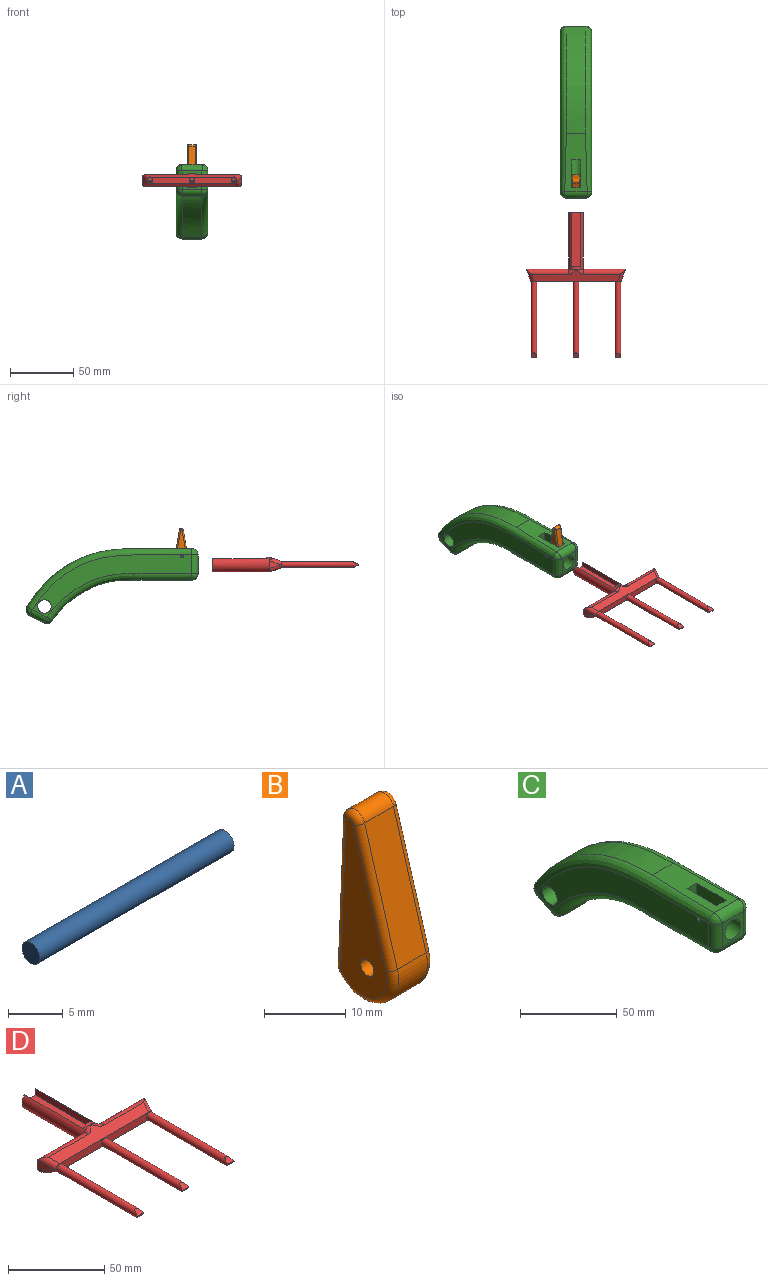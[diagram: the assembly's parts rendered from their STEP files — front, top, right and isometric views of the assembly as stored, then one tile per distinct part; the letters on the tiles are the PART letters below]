
ASSEMBLY  parts=4 mates=3
PART A: 3 faces, bbox 25x2.3x2.3 mm
  f0: cylinder r=1.14mm len=25mm, axis (1,0,0), area 179.2mm2, adj f1,f2
  f1: plane 2.28x2.28mm, normal (-1,0,0), area 4.1mm2, adj f0
  f2: plane 2.28x2.28mm, normal (1,0,0), area 4.1mm2, adj f0
PART B: 15 faces, bbox 7x10.9x27.8 mm
  f0: plane 19.22x5.69mm, normal (0,-0.96,0.28), area 100.2mm2, adj f1,f3,f8,f12
  f1: cylinder r=5.38mm len=10.09mm, axis (-1,0,0), area 78.7mm2, adj f0,f2,f10,f14
  f2: plane 23.45x5mm, normal (0,1,0.04), area 117.4mm2, adj f1,f3,f9,f13
  f3: cylinder r=1.69mm len=5mm, axis (-1,0,0), area 21.2mm2, adj f0,f2,f7,f11
  f4: plane 25.34x8.08mm, normal (1,0,0), area 121.9mm2, adj f6,f11,f12,f13,f14
  f5: plane 25.34x8.08mm, normal (-1,0,0), area 121.9mm2, adj f6,f7,f8,f9,f10
  f6: cylinder r=1.14mm len=7mm, axis (-1,0,0), area 50.2mm2, adj f4,f5
  f7: torus R=0.69mm, axis (1,0,0), area 5.1mm2, adj f3,f5,f8,f9
  f8: cylinder r=1mm len=19.5mm, axis (0,-0.28,-0.96), area 31.5mm2, adj f0,f5,f7,f10
  f9: cylinder r=1mm len=23.49mm, axis (0,-0.04,1), area 36.6mm2, adj f2,f5,f7,f10
  f10: torus R=4.38mm, axis (1,0,0), area 22.9mm2, adj f1,f5,f8,f9
  f11: torus R=0.69mm, axis (1,0,0), area 5.1mm2, adj f3,f4,f12,f13
  f12: cylinder r=1mm len=19.5mm, axis (0,0.28,0.96), area 31.5mm2, adj f0,f4,f11,f14
  f13: cylinder r=1mm len=23.49mm, axis (0,0.04,-1), area 36.6mm2, adj f2,f4,f11,f14
  f14: torus R=4.38mm, axis (1,0,0), area 22.9mm2, adj f1,f4,f12,f13
PART C: 42 faces, bbox 25.7x249.5x60.2 mm
  f0: plane 21.69x7.76mm, normal (-1,0,0), area 164.2mm2, adj f1,f2,f3,f36,f40
  f1: plane 46.77x18.22mm, normal (0,0,1), area 618.5mm2, adj f0,f3,f4,f22,f25,f26,f34,f35
  f2: cylinder r=5.84mm len=30mm, axis (0,-1,0), area 937.3mm2, adj f0,f3,f5,f36,f37
  f3: plane 18.26x11.67mm, normal (0,-1,0), area 155.8mm2, adj f0,f1,f2,f37
  f4: extruded ~83.73x45.57mm, area 1502.9mm2, adj f1,f16,f22,f25
  f5: plane 15x14.86mm, normal (0,-1,0), area 115.9mm2, adj f2,f19,f23,f24,f26
  f6: plane 45.58x15mm, normal (0,0,-1), area 683.7mm2, adj f19,f28,f30,f33
  f7: extruded ~64.24x32.08mm, area 1126mm2, adj f11,f18,f20,f30
  f8: plane 15x11.42mm, normal (0,0.45,-0.89), area 191.8mm2, adj f11,f12,f15,f16
  f9: plane 125.62x49.15mm, normal (1,0,0), area 1800.3mm2, adj f12,f18,f22,f23,f28,f40,f41
  f10: plane 125.62x49.16mm, normal (-1,0,0), area 1836.8mm2, adj f15,f20,f24,f25,f33,f38,f39
  f11: cylinder r=5mm len=15mm, axis (-1,0,0), area 107.1mm2, adj f7,f8,f13,f14
  f12: cylinder r=5mm len=13.67mm, axis (0,-0.89,-0.45), area 100.4mm2, adj f8,f9,f13,f17
  f13: sphere r=5mm, area 34.3mm2, adj f11,f12,f18
  f14: sphere r=5mm, area 40.8mm2, adj f11,f15,f20
  f15: cylinder r=5mm len=13.67mm, axis (0,0.89,0.45), area 100.4mm2, adj f8,f10,f14,f21
  f16: cylinder r=5mm len=15mm, axis (-1,0,0), area 124.5mm2, adj f4,f8,f17,f21
  f17: sphere r=5mm, area 33.5mm2, adj f12,f16,f22
  f18: bspline ~71.25x38.86mm, area 604mm2, adj f7,f9,f13,f29
  f19: cylinder r=5mm len=15mm, axis (-1,0,0), area 117.8mm2, adj f5,f6,f27,f31
  f20: bspline ~71.25x38.86mm, area 604mm2, adj f7,f10,f14,f32
  f21: sphere r=5mm, area 30.2mm2, adj f15,f16,f25
  f22: bspline ~248.79x52.38mm, area 1105mm2, adj f1,f4,f9,f17,f34
  f23: cylinder r=5mm len=15.02mm, axis (0,0,1), area 118mm2, adj f5,f9,f26,f27,f34
  f24: cylinder r=5mm len=15.02mm, axis (0,0,-1), area 118mm2, adj f5,f10,f26,f31,f35
  f25: bspline ~248.79x52.38mm, area 1105mm2, adj f1,f4,f10,f21,f35
  f26: cylinder r=5mm len=17.56mm, axis (1,0,0), area 133mm2, adj f1,f5,f23,f24,f34,f35
  f27: sphere r=5mm, area 39.3mm2, adj f19,f23,f28
  f28: cylinder r=5mm len=45.58mm, axis (0,1,0), area 358mm2, adj f6,f9,f27,f29
  f29: sphere r=5mm, area 1.3mm2, adj f18,f28,f30
  f30: cylinder r=5mm len=15mm, axis (-1,0,0), area 3.8mm2, adj f6,f7,f29,f32
  f31: sphere r=5mm, area 39.3mm2, adj f19,f24,f33
  f32: sphere r=5mm, area 1.3mm2, adj f20,f30,f33
  f33: cylinder r=5mm len=45.58mm, axis (0,1,0), area 358mm2, adj f6,f10,f31,f32
  f34: sphere r=5mm, area 31.6mm2, adj f1,f22,f23,f26
  f35: sphere r=5mm, area 31.6mm2, adj f1,f24,f25,f26
  f36: plane 7.76x7mm, normal (0,1,0), area 48.7mm2, adj f0,f1,f2,f37
  f37: plane 21.69x7.76mm, normal (1,0,0), area 164.2mm2, adj f1,f2,f3,f36,f39
  f38: cylinder r=5.31mm len=24mm, axis (1,0,0), area 800.2mm2, adj f10,f41
  f39: cylinder r=1.14mm len=9mm, axis (1,0,0), area 64.5mm2, adj f10,f37
  f40: cylinder r=1.14mm len=9mm, axis (1,0,0), area 64.5mm2, adj f0,f9
  f41: torus R=6.31mm, axis (1,0,0), area 56mm2, adj f9,f38
PART D: 37 faces, bbox 78.9x115.2x12.8 mm
  f0: cylinder r=2.25mm len=60mm, axis (0,1,0), area 817.5mm2, adj f1,f19,f35,f36
  f1: plane 4.5x0.65mm, normal (0,-1,0), area 2.9mm2, adj f0,f35,f36
  f2: cylinder r=2.25mm len=60mm, axis (0,1,0), area 817.5mm2, adj f3,f19,f33,f34
  f3: plane 4.5x0.65mm, normal (0,-1,0), area 2.9mm2, adj f2,f33,f34
  f4: cylinder r=2.25mm len=60mm, axis (0,1,0), area 817.5mm2, adj f5,f19,f31,f32
  f5: plane 4.5x0.65mm, normal (0,-1,0), area 2.9mm2, adj f4,f31,f32
  f6: plane 33.66x3.52mm, normal (0,1,0), area 117.7mm2, adj f11,f18,f22,f25
  f7: plane 8.13x1.89mm, normal (0,1,0), area 0.2mm2, adj f13,f24
  f8: plane 42.51x4.01mm, normal (-1,0,0), area 170.5mm2, adj f9,f11,f12,f14
  f9: plane 42.51x7.71mm, normal (0,0,1), area 327.9mm2, adj f8,f10,f12,f14
  f10: plane 42.51x3.99mm, normal (1,0,0), area 169.5mm2, adj f9,f11,f12,f14
  f11: cylinder r=5.82mm len=44.51mm, axis (0,1,0), area 1252.2mm2, adj f6,f8,f10,f12,f13,f20,f24,f27
  f12: plane 11.64x10.19mm, normal (0,1,0), area 67.8mm2, adj f8,f9,f10,f11
  f13: cylinder r=5.96mm len=7.71mm, axis (0,-1,0), area 16.8mm2, adj f7,f11,f14
  f14: plane 7.71x5.42mm, normal (0,1,0), area 38.3mm2, adj f8,f9,f10,f13
  f15: plane 69.72x8.49mm, normal (0,-0.34,-0.94), area 442.5mm2, adj f19,f23,f25,f27,f29,f30
  f16: plane 8.92x6.28mm, normal (0.94,-0.34,0), area 30.1mm2, adj f20,f26,f28,f29,f30
  f17: plane 69.72x9.51mm, normal (0,-0.34,0.94), area 446.4mm2, adj f19,f21,f22,f24,f26,f28
  f18: plane 8.92x6.28mm, normal (-0.94,-0.34,0), area 30.1mm2, adj f6,f21,f22,f23,f25
  f19: plane 71.6x5.46mm, normal (0,-1,0), area 287.5mm2, adj f0,f2,f4,f15,f17,f21,f23,f28
  f20: plane 33.66x3.52mm, normal (0,1,0), area 117.7mm2, adj f11,f16,f26,f29
  f21: cylinder r=3mm len=10.03mm, axis (-0.32,0.89,0.32), area 39.9mm2, adj f17,f18,f19,f22,f23
  f22: cylinder r=3mm len=33.54mm, axis (1,0,0), area 185.5mm2, adj f6,f17,f18,f21,f24
  f23: cylinder r=3mm len=10.03mm, axis (-0.32,0.89,-0.32), area 39.9mm2, adj f15,f18,f19,f21,f25
  f24: bspline ~11.54x4.33mm, area 33.1mm2, adj f7,f11,f17,f22,f26
  f25: cylinder r=3mm len=33.66mm, axis (1,0,0), area 186.2mm2, adj f6,f15,f18,f23,f27
  f26: cylinder r=3mm len=33.54mm, axis (1,0,0), area 185.5mm2, adj f16,f17,f20,f24,f28
  f27: bspline ~11.27x4.36mm, area 35.9mm2, adj f11,f15,f25,f29
  f28: cylinder r=3mm len=10.03mm, axis (0.32,0.89,0.32), area 39.9mm2, adj f16,f17,f19,f26,f30
  f29: cylinder r=3mm len=33.66mm, axis (1,0,0), area 186.2mm2, adj f15,f16,f20,f27,f30
  f30: cylinder r=3mm len=10.03mm, axis (0.32,0.89,-0.32), area 39.9mm2, adj f15,f16,f19,f28,f29
  f31: plane 4.42x3.6mm, normal (0,-0.45,-0.89), area 13.4mm2, adj f4,f5
  f32: plane 4.48x3.85mm, normal (0,-0.46,0.89), area 14.9mm2, adj f4,f5
  f33: plane 4.41x3.54mm, normal (0,-0.45,-0.89), area 13.1mm2, adj f2,f3
  f34: plane 4.48x3.91mm, normal (0,-0.46,0.89), area 15.2mm2, adj f2,f3
  f35: plane 4.41x3.54mm, normal (0,-0.45,-0.89), area 13.1mm2, adj f0,f1
  f36: plane 4.48x3.91mm, normal (0,-0.46,0.89), area 15.2mm2, adj f0,f1
PLACE A t=(-4.83,50.71,-47.53)mm
PLACE B rot(axis=(1,0,0),6.7deg) t=(-4.83,55.8,-42.79)mm
PLACE C t=(-4.83,50.71,-47.53)mm
PLACE D t=(-4.83,54.73,-47.53)mm
MATE revolute A.f0 <-> C.f39  axis (1,0,0) through (20.17,12.53,-1.38)mm
MATE slider D.f11 <-> C.f2  axis (0,1,0) through (7.67,-11.46,-7.59)mm
MATE revolute B.f6 <-> C.f39  axis (-1,0,0) through (4.17,12.53,-1.38)mm
